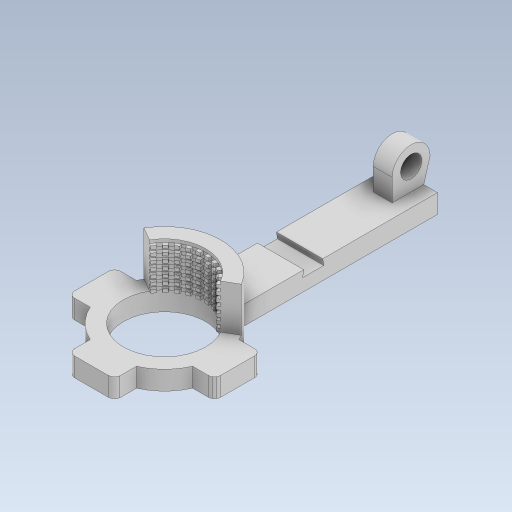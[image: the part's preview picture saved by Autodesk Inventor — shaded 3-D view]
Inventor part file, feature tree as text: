
AUTODESK INVENTOR PART (.ipt)
format: ipt  version: 2023 (Build 270158000, 158)  size: 558,080 bytes
history: native  units: in
note: dims shown in document units (in); Inventor stores cm internally (conversion verified against a paired STEP export)
features: sketch x10, extrude x8, revolve x1, hole x1, mirror x1, projected_geometry x1
ambient origin geometry x8: Origin, YZ Plane, XZ Plane, XY Plane, X Axis, Y Axis, Z Axis, Center Point
bodies: Solid1 (feature_tree)
feature tree (22):
  extrude  "Extrusion1"  Depth=0.2362in TaperAngle=0.0deg
  extrude  "Extrusion2"  Depth=0.5512in TaperAngle=0.0deg
  extrude  "Extrusion3"  Depth=0.0394in TaperAngle=120.0deg
  revolve  "Revolution1"  [1 undecoded]
  extrude  "Extrusion4"  Depth=0.1969in TaperAngle=0.0deg
  extrude  "Extrusion5"  Depth=0.2362in
  extrude  "Extrusion6"  Depth=0.0787in
  hole  "Hole1"  [1 undecoded]
  mirror  "Mirror1"
  extrude  "Extrusion7"  Depth=0.2756in
  extrude  "Extrusion8"  Depth=0.0787in
  sketch  "Sketch1"  dims[d0=1.0236in d1=0.2362in d2=0.0in]
  sketch  "Sketch2"  dims[d3=120.0deg d4=0.5512in d5=0.0in]
  sketch  "Sketch3"  dims[d6=0.0394in d7=7.874in d9=120.0deg]
  sketch  "Sketch4"  dims[d11=0.3937in d12=0.0in d14=5.5118in d16=0.0394in d17=0.3937in d19=0.3937in]
  sketch  "Sketch5"  dims[d21=360.0deg d22=2.2835in d23=0.1969in d24=0.0in d25=0.0in]
  sketch  "Sketch6"  dims[d26=0.2362in d27=1.4479in]
  sketch  "Sketch7"  dims[d28=1.3998in d29=0.0787in d30=0.0687in]
  sketch  "Sketch8"  dims[d31=0.2362in d32=0.4724in]
  sketch  "Sketch9"  dims[d33=0.5906in d34=0.0in d35=0.2756in]
  sketch  "Sketch10"  dims[d36=0.266in d37=0.2362in d38=0.1575in d39=0.0787in d40=90.0deg d41=0.315in d42=0.8108in d43=0.0787in d44=0.7874in d46=90.0deg d48=0.0in d49=0.0in d50=0.0787in d51=0.0in d52=0.0in]
  projected_geometry  "Projected Loop1"
note: 2 required parameter values undecoded (feature->parameter linkage not recoverable at this tier; creation-order binding heuristic only, values carry confidence <= 0.55)